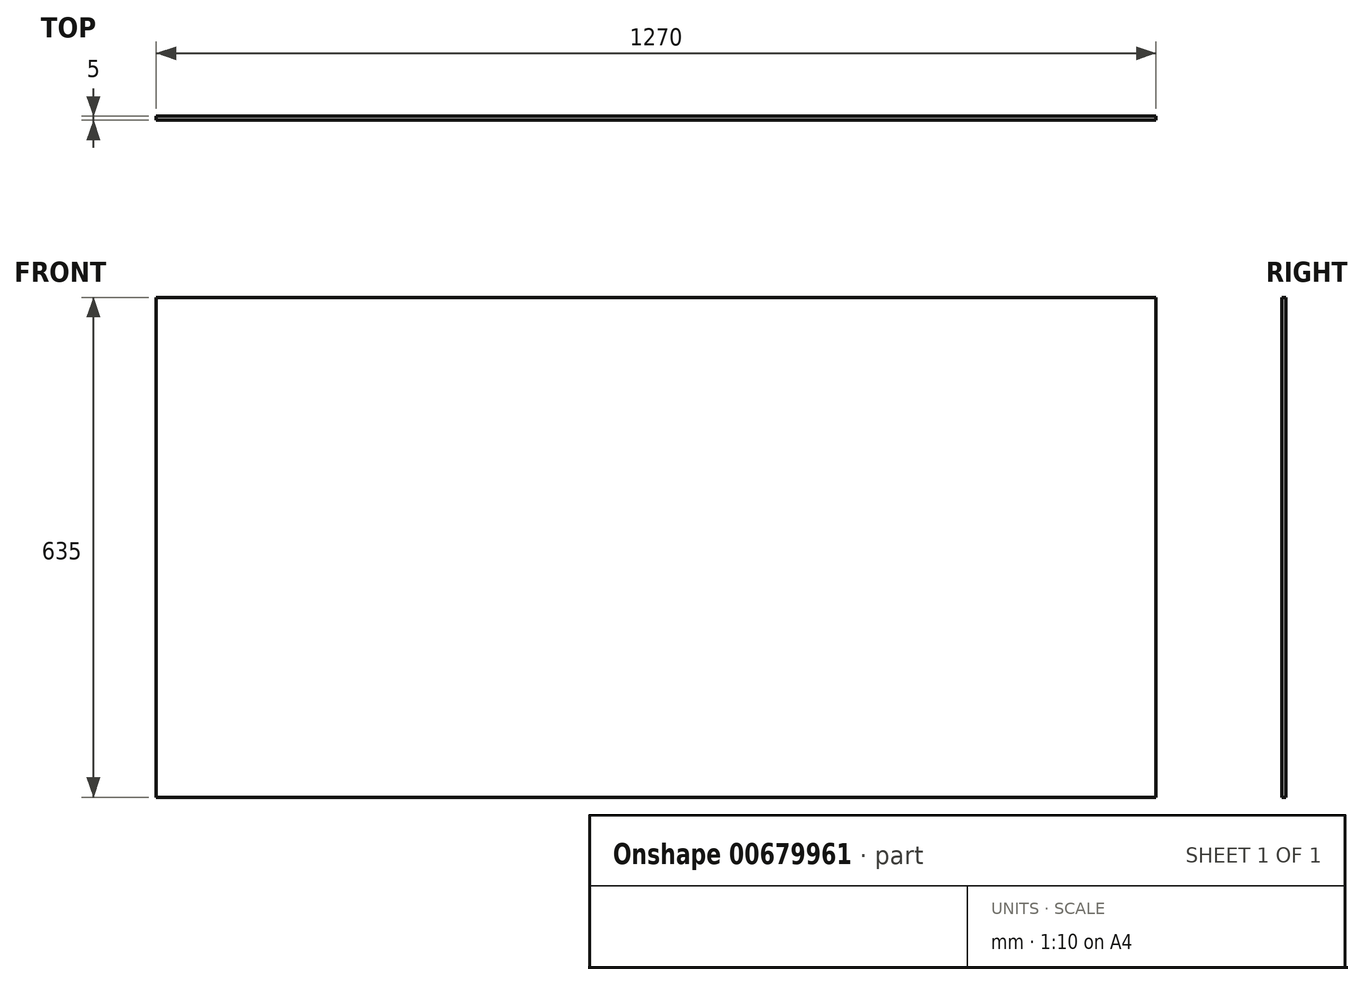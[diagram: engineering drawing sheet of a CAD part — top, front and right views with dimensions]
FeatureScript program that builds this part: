
annotation { "Feature Type Name" : "Feature", "Feature Type Description" : "" }
export const myFeature = defineFeature(function(context is Context, id is Id, definition is map)
    precondition{}
    {
        {
            assignVariable(context, id + "F0", {"name" : "extrude", "anyValue" : 5});
        }
        {
            var Q0;
            Q0=qCreatedBy(makeId("Front.planeOp"),FACE);
            var sketch = newSketch(context, id + "F1", { "sketchPlane" : qUnion([Q0])});
            skLineSegment(sketch, "E0.bottom", {"start": v(0, 0) * mm, "end": v(-1270, 0) * mm});
            skLineSegment(sketch, "E0.top", {"start": v(0, 635) * mm, "end": v(-1270, 635) * mm});
            skLineSegment(sketch, "E0.left", {"start": v(0, 0) * mm, "end": v(0, 635) * mm});
            skLineSegment(sketch, "E0.right", {"start": v(-1270, 0) * mm, "end": v(-1270, 635) * mm});
            skSolve(sketch);
        }
        {
            var Q0;
            Q0 = qSketchRegion(id + "F1", true);
            extrude(context, id + "F2", {"entities" : qUnion([Q0]), "depth" : (getVariable(context, 'extrude')) * mm, "offsetDistance" : 25.4 * mm});
        }
    });
